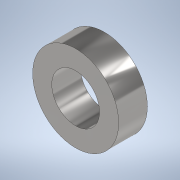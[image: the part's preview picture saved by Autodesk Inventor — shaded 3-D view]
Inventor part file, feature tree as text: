
AUTODESK INVENTOR PART (.ipt)
format: ipt  version: 2022 (Build 260153000, 153)  size: 104,448 bytes
history: native  units: in
note: dims shown in document units (in); Inventor stores cm internally (conversion verified against a paired STEP export)
features: extrude x1, sketch x1
ambient origin geometry x8: Origin, YZ Plane, XZ Plane, XY Plane, X Axis, Y Axis, Z Axis, Center Point
bodies: Solid1 (feature_tree)
feature tree (2):
  extrude  "Extrusion1"  Depth=0.1181in
  sketch  "Sketch1"  dims[d0=0.3543in d1=0.1969in d2=0.1181in d3=0.0in]
